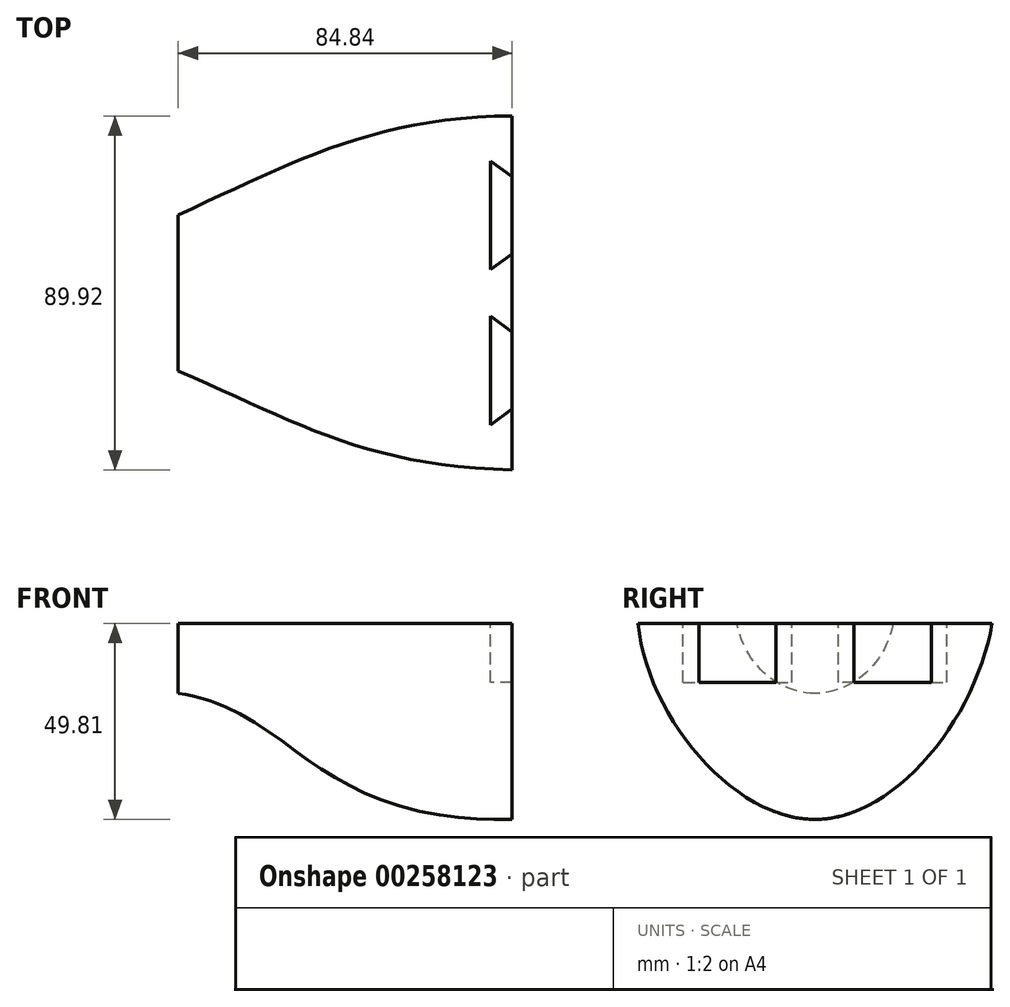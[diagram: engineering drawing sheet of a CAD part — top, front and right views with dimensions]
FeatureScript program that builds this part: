
annotation { "Feature Type Name" : "Feature", "Feature Type Description" : "" }
export const myFeature = defineFeature(function(context is Context, id is Id, definition is map)
    precondition{}
    {
        {
            var Q0;
            Q0=qCreatedBy(makeId("Right.planeOp"),FACE);
            var sketch = newSketch(context, id + "F0", { "sketchPlane" : qUnion([Q0])});
            skPoint(sketch, "E0", {"position": v(-44.96, 0) * mm});
            skPoint(sketch, "E1", {"position": v(44.96, 0) * mm});
            skPoint(sketch, "E2", {"position": v(0, -49.78) * mm});
            skFitSpline(sketch, "E3", {"points": [v(-44.96, 0) * mm, v(0, -49.78) * mm, v(44.96, 0) * mm], "startDerivative": vector(13.46, -141.06) * mm, "endDerivative": vector(23.12, 139.97) * mm});
            skLineSegment(sketch, "E4", {"start": v(-44.96, 0) * mm, "end": v(44.96, 0) * mm});
            skSolve(sketch);
        }
        {
            var Q0;
            Q0=qCreatedBy(makeId("Right.planeOp"),FACE);
            cPlane(context, id + "F1", {"entities" : qUnion([Q0]), "cplaneType" : CPlaneType.OFFSET, "offset" : 84.84 * mm, "oppositeDirection" : true, "width" : 152.4 * mm, "height" : 152.4 * mm});
        }
        {
            var Q0;
            Q0=qCreatedBy(id+"F1.planeOp",FACE);
            var sketch = newSketch(context, id + "F2", { "sketchPlane" : qUnion([Q0])});
            skPoint(sketch, "E5", {"position": v(19.81, 0) * mm});
            skPoint(sketch, "E6", {"position": v(-19.81, 0) * mm});
            skPoint(sketch, "E7", {"position": v(0, -17.78) * mm});
            skFitSpline(sketch, "E8", {"points": [v(19.81, 0) * mm, v(0, -17.78) * mm, v(-19.81, 0) * mm], "startDerivative": vector(-12.2, -64.7) * mm, "endDerivative": vector(-12.2, 64.7) * mm});
            skLineSegment(sketch, "E9", {"start": v(19.81, 0) * mm, "end": v(-19.81, 0) * mm});
            skSolve(sketch);
        }
        {
            var Q0;
            Q0=qCreatedBy(makeId("Top.planeOp"),FACE);
            var sketch = newSketch(context, id + "F3", { "sketchPlane" : qUnion([Q0])});
            skFitSpline(sketch, "E10", {"points": [v(0, -44.96) * mm, v(-84.84, -19.81) * mm], "startDerivative": vector(-112.4, 2.98) * mm, "endDerivative": vector(-90.21, 38.86) * mm});
            skFitSpline(sketch, "E11", {"points": [v(0, 44.96) * mm, v(-84.84, 19.81) * mm], "startDerivative": vector(-104.47, 0) * mm, "endDerivative": vector(-85.02, -38.86) * mm});
            skPoint(sketch, "E12", {"position": v(-46.86, 0) * mm});
            skPoint(sketch, "E13", {"position": v(-48.84, 0) * mm});
            skSolve(sketch);
        }
        {
            var Q0;
            Q0=qCreatedBy(makeId("Front.planeOp"),FACE);
            var sketch = newSketch(context, id + "F4", { "sketchPlane" : qUnion([Q0])});
            skFitSpline(sketch, "E14", {"points": [v(0, -49.78) * mm, v(-84.84, -17.78) * mm], "startDerivative": vector(-152.72, -3.07) * mm, "endDerivative": vector(-88.92, 12.13) * mm});
            skSolve(sketch);
        }
        {
            var Q0;
            Q0=makeQuery(id+"F0.imprint","IMPRINT",FACE,{"disambiguationData":[TD([[makeQuery(id+"F0.imprint","IMPRINT",EDGE,{"derivedFrom":sQuery(id+"F0.wireOp",EDGE,"E3")}),1.0]])]});
            var Q1;
            Q1=makeQuery(id+"F2.imprint","IMPRINT",FACE,{"disambiguationData":[TD([[makeQuery(id+"F2.imprint","IMPRINT",EDGE,{"derivedFrom":sQuery(id+"F2.wireOp",EDGE,"E8")}),-1.0]])]});
            var Q2;
            Q2=sQuery(id+"F4.wireOp",EDGE,"E14");
            var Q3;
            Q3=sQuery(id+"F3.wireOp",EDGE,"E10");
            var Q4;
            Q4=sQuery(id+"F3.wireOp",EDGE,"E11");
            loft(context, id + "F5", {"addGuides" : true, "sheetProfilesArray" : [{ "sheetProfileEntities" : qUnion([Q0]) }, { "sheetProfileEntities" : qUnion([Q1]) }], "guidesArray" : [{ "guideEntities" : qUnion([Q2]), "guideDerivativeType" : LoftGuideDerivativeType.DEFAULT, "guideDerivativeMagnitude" : 1 }, { "guideEntities" : qUnion([Q3]), "guideDerivativeType" : LoftGuideDerivativeType.DEFAULT, "guideDerivativeMagnitude" : 1 }, { "guideEntities" : qUnion([Q4]), "guideDerivativeType" : LoftGuideDerivativeType.DEFAULT, "guideDerivativeMagnitude" : 1 }]});
        }
        {
            var Q0;
            Q0=makeQuery(id+"F5.opLoft","SWEPT_FACE",FACE,{"disambiguationData":[OSD([sQuery(id+"F0.wireOp",EDGE,"E4"),sQuery(id+"F2.wireOp",EDGE,"E8"),sQuery(id+"F2.wireOp",EDGE,"E9"),sQuery(id+"F3.wireOp",EDGE,"E10"),sQuery(id+"F3.wireOp",EDGE,"E11")])]});
            var sketch = newSketch(context, id + "F6", { "sketchPlane" : qUnion([Q0])});
            skLineSegment(sketch, "E15", {"start": v(0, 29.52) * mm, "end": v(-5.47, 33.55) * mm});
            skLineSegment(sketch, "E16", {"start": v(-5.47, 33.55) * mm, "end": v(-5.47, 19.73) * mm});
            skLineSegment(sketch, "E17.MirrorCS", {"start": v(-5.47, 5.9) * mm, "end": v(-5.47, 19.73) * mm});
            skLineSegment(sketch, "E18.MirrorCS", {"start": v(0, 9.94) * mm, "end": v(-5.47, 5.9) * mm});
            skSolve(sketch);
        }
        {
            var Q0;
            {var subQ1=sQuery(id+"F6.wireOp",EDGE,"E15");Q0=makeQuery(id+"F6.imprint","IMPRINT",FACE,{"disambiguationData":[TD([[makeQuery(id+"F6.imprint","IMPRINT",EDGE,{"derivedFrom":subQ1}),1.0]])]});}
            extrude(context, id + "F7", {"entities" : qUnion([Q0]), "operationType" : NewBodyOperationType.REMOVE, "oppositeDirection" : true, "depth" : 15 * mm});
        }
        {
            var Q0;
            Q0=makeQuery(id+"F5.opLoft","SWEPT_FACE",FACE,{"disambiguationData":[OSD([sQuery(id+"F0.wireOp",EDGE,"E4"),sQuery(id+"F2.wireOp",EDGE,"E8"),sQuery(id+"F2.wireOp",EDGE,"E9"),sQuery(id+"F3.wireOp",EDGE,"E10"),sQuery(id+"F3.wireOp",EDGE,"E11")])]});
            var sketch = newSketch(context, id + "F8", { "sketchPlane" : qUnion([Q0])});
            skLineSegment(sketch, "E19", {"start": v(0, -9.93) * mm, "end": v(-5.47, -5.9) * mm});
            skLineSegment(sketch, "E20", {"start": v(-5.47, -21.63) * mm, "end": v(-5.47, -5.9) * mm});
            skLineSegment(sketch, "E21.MirrorCS", {"start": v(0, -29.51) * mm, "end": v(-5.47, -33.57) * mm});
            skLineSegment(sketch, "E22.MirrorCS", {"start": v(-5.47, -16.37) * mm, "end": v(-5.47, -33.57) * mm});
            skSolve(sketch);
        }
        {
            var Q0;
            {var subQ4=sQuery(id+"F8.wireOp",EDGE,"E19");Q0=makeQuery(id+"F8.imprint","IMPRINT",FACE,{"disambiguationData":[TD([[makeQuery(id+"F8.imprint","IMPRINT",EDGE,{"derivedFrom":subQ4}),1.0]])]});}
            extrude(context, id + "F9", {"entities" : qUnion([Q0]), "operationType" : NewBodyOperationType.REMOVE, "oppositeDirection" : true, "depth" : 15 * mm});
        }
    });
